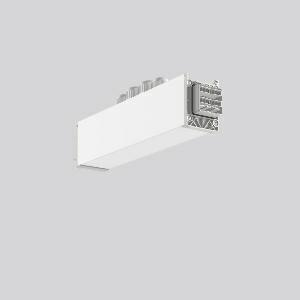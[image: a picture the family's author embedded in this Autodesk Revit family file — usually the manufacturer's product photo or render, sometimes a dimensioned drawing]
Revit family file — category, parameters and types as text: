
# Revit family: linedo_mitteleinspeisung_7pol_s_s_982698_002_5_233b
name_source: partatom
category: Lighting Fixtures
units: mm (PartAtom-declared; Revit-internal decimal feet)

## family parameters
Cut with Voids When Loaded = No
Host = Face
Light Source = No
Part Type = Normal
Room Calculation Point = No
Round Connector Dimension = Use Diameter
Shared = No

## types (1)
- LINEDO_Mitteleinspeisung_7pol_S_S
    Apparent Load = 0 VA
    Default Elevation = 1800 mm
    Description = Series: LINEDO
Middle power feed, 7-pole, connection plug / plug. Housing: extruded aluminium profile, powder-coated. Cover made of plastic, surface like housing. LINEDO plug system, plastic, light grey. 4 cable glands (2 x M20 and 2 x M25). Cable glands on top. Easy connection for rigid or flexible wires.
Colour: white
Length: 349 mm
Width: 58 mm
Height: 76 mm
Weight: 751 g
    Height = 76 mm
    Lamp = 0 x
    Length = 349 mm
    Luminous efficacy = 0 lm/W
    Manufacturer = RZB
    ModVariant = No
    Model = 982698.002.5
    Mounting Place = Ceiling
    Mounting Type = Surface mounted, Pendant
    Number of Poles = 1
    OnlyDefault = Yes
    Power Factor = 1
    Product Name = LINEDO_Mitteleinspeisung_7pol_S_S
    Product group = Surface mounted continuous line luminaire system
    ProductGroupID = 310
    Protection Class = Protection class I
    Protection Degree = IP 54
    RLX_Detail_Level = 1
    RLX_Emergency_Light_Flux = 0 lm
    RLX_Emergency_Type = 0
    RLX_Emergency_Type_DB = No
    RlxData = <blob elided: 20765 chars, md5=f78f7859>
    Standby Power = 0 W
    System Light Flux = 0 lm
    System Power = 0 W
    Type Comments = Product without accessories
    Type Image = 982698.002.2.jpg
    URL = http://relux.com
    VarID = ---
    Voltage = 0 V
    Weight = 0.00 kg
    Width = 58 mm

## geometry (parser evidence)
native form markers: Blend x4, Sweep x10
no freeform markers — native parametric forms only
